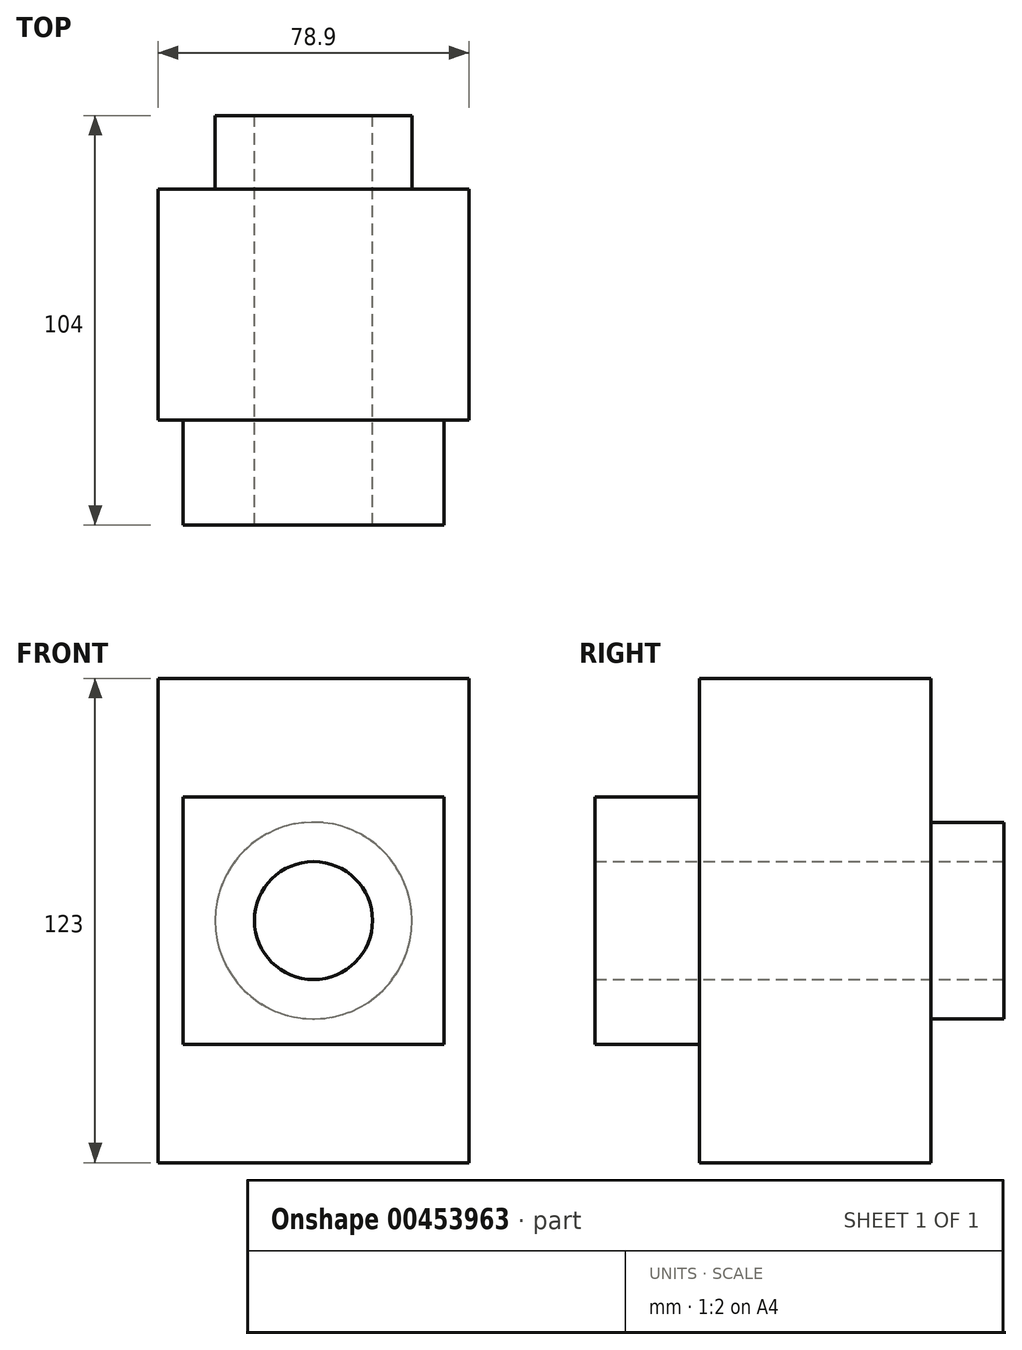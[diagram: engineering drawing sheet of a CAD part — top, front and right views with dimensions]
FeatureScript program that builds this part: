
annotation { "Feature Type Name" : "Feature", "Feature Type Description" : "" }
export const myFeature = defineFeature(function(context is Context, id is Id, definition is map)
    precondition{}
    {
        {
            var Q0;
            Q0=qCreatedBy(makeId("Front.planeOp"),FACE);
            var sketch = newSketch(context, id + "F0", { "sketchPlane" : qUnion([Q0])});
            skCircle(sketch, "E0", {"center": v(0, 0) * mm, "radius": 25 * mm});
            skSolve(sketch);
        }
        {
            var Q0;
            Q0=makeQuery(id+"F0.imprint","IMPRINT",FACE,{"disambiguationData":[TD([[makeQuery(id+"F0.imprint","IMPRINT",EDGE,{"derivedFrom":sQuery(id+"F0.wireOp",EDGE,"E0")}),1.0]])]});
            extrude(context, id + "F1", {"entities" : qUnion([Q0]), "oppositeDirection" : true, "depth" : 48 * mm});
        }
        {
            var Q0;
            Q0=qCreatedBy(makeId("Front.planeOp"),FACE);
            var sketch = newSketch(context, id + "F2", { "sketchPlane" : qUnion([Q0])});
            skLineSegment(sketch, "E1.bottom", {"start": v(-33.19, 31.45) * mm, "end": v(33.19, 31.45) * mm});
            skLineSegment(sketch, "E1.top", {"start": v(-33.19, -31.45) * mm, "end": v(33.19, -31.45) * mm});
            skLineSegment(sketch, "E1.left", {"start": v(-33.19, 31.45) * mm, "end": v(-33.19, -31.45) * mm});
            skLineSegment(sketch, "E1.right", {"start": v(33.19, 31.45) * mm, "end": v(33.19, -31.45) * mm});
            skPoint(sketch, "E1.middle", {"position": v(0, 0) * mm});
            skSolve(sketch);
        }
        {
            var Q0;
            Q0=makeQuery(id+"F2.imprint","IMPRINT",FACE,{"disambiguationData":[TD([[makeQuery(id+"F2.imprint","IMPRINT",EDGE,{"derivedFrom":sQuery(id+"F2.wireOp",EDGE,"E1.bottom")}),-1.0]])]});
            extrude(context, id + "F3", {"entities" : qUnion([Q0]), "operationType" : NewBodyOperationType.ADD, "depth" : 56 * mm});
        }
        {
            var Q0;
            Q0=qCreatedBy(makeId("Top.planeOp"),FACE);
            var sketch = newSketch(context, id + "F4", { "sketchPlane" : qUnion([Q0])});
            skLineSegment(sketch, "E2.bottom", {"start": v(39.45, -29.37) * mm, "end": v(-39.45, -29.37) * mm});
            skLineSegment(sketch, "E2.top", {"start": v(39.45, 29.37) * mm, "end": v(-39.45, 29.37) * mm});
            skLineSegment(sketch, "E2.left", {"start": v(39.45, -29.37) * mm, "end": v(39.45, 29.37) * mm});
            skLineSegment(sketch, "E2.right", {"start": v(-39.45, -29.37) * mm, "end": v(-39.45, 29.37) * mm});
            skPoint(sketch, "E2.middle", {"position": v(0, 0) * mm});
            skSolve(sketch);
        }
        {
            var Q0;
            Q0=makeQuery(id+"F4.imprint","IMPRINT",FACE,{"disambiguationData":[TD([[makeQuery(id+"F4.imprint","IMPRINT",EDGE,{"derivedFrom":sQuery(id+"F4.wireOp",EDGE,"E2.bottom")}),-1.0]])]});
            extrude(context, id + "F5", {"entities" : qUnion([Q0]), "operationType" : NewBodyOperationType.ADD, "endBound" : BoundingType.SYMMETRIC, "oppositeDirection" : true, "depth" : 123 * mm});
        }
        {
            var Q0;
            Q0=makeQuery(id+"F1.opExtrude","CAP_FACE",FACE,{"disambiguationData":[OSD([sQuery(id+"F0.wireOp",EDGE,"E0")])],"isStart":false});
            var sketch = newSketch(context, id + "F6", { "sketchPlane" : qUnion([Q0])});
            skCircle(sketch, "E3", {"center": v(0, 0) * mm, "radius": 15 * mm});
            skSolve(sketch);
        }
        {
            var Q0;
            Q0=makeQuery(id+"F6.imprint","IMPRINT",FACE,{"disambiguationData":[TD([[makeQuery(id+"F6.imprint","IMPRINT",EDGE,{"derivedFrom":sQuery(id+"F6.wireOp",EDGE,"E3")}),1.0]])]});
            extrude(context, id + "F7", {"entities" : qUnion([Q0]), "operationType" : NewBodyOperationType.REMOVE, "oppositeDirection" : true, "depth" : 105.3 * mm});
        }
    });
